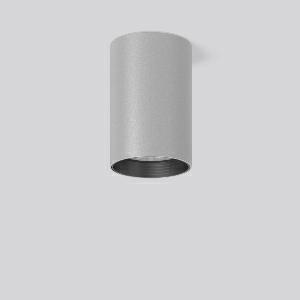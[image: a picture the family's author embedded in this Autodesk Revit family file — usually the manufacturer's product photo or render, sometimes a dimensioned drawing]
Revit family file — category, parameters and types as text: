
# Revit family: heledon_maxi_a_931229_004_3_d102
name_source: partatom
category: Lighting Fixtures
units: mm (PartAtom-declared; Revit-internal decimal feet)

## family parameters
Cut with Voids When Loaded = No
Host = Face
Light Source = No
Part Type = Normal
Room Calculation Point = No
Round Connector Dimension = Use Diameter
Shared = No

## types (1)
- HELEDON maxi A (1 x LED Modul 935, 3650 lm, 3500)
    Apparent Load = 35 VA
    Approval mark = CE
    CIE Flux Codes = 96 100 100 100 100
    Color Rendering = 92
    Color Temperature = 3500
    Default Elevation = 1800 mm
    Description = Series: HELEDON maxi
Cylindrical surface-mounted downlight. Housing: die-cast aluminium, powder-coated. Internal ceiling frame polycarbonate with bayonet mounting. Black plastic ring and recessed LED to prevent glare from the side. Optical assembly with lens made of plastic (polycarbonate) for the best homogeneous light distribution - can be changed without tools. Best colour rendering index Ra>90. Suitable for Ceiling mounting. Easy installation with a separate ceiling frame with bayonet mounting and plug connection. Driver integrated. Connected via plug-in connector. High quality converter without flickering and stroboscopic effect. The following accessories can be mounted without use of tools: interchangeable lenses, decorative glasses, honeycomb louvre, clear and frosted diffusers, white interchangeable plastic ring. 
Colour: silver
Diameter: 123 mm
Height: 183 mm
Lamp: LED
Socket: without socket
Colour temperature: 3500K
Colour rendering index (CRI): 92
System power: 35 W
Rated luminous flux: 3650 lm
Luminous efficiency: 104 lm/W
Control gear: Regulated power supply
Protection class: I
Type of protection: IP 20
    Height = 183 mm
    Lamp = 1 x LED Modul 935
    Lamp Light Flux = 3650 lm
    Lamp count = 1
    Length = 123 mm
    Lifetime = 50000 h
    Luminous efficacy = 104 lm/W
    Manufacturer = RZB
    ModVariant = No
    Model = 931229.004.3
    Mounting Place = Ceiling
    Mounting Type = Surface mounted
    Number of Poles = 1
    OnlyDefault = Yes
    Power Factor = 1
    Product Name = HELEDON maxi A
    Product group = Surface mounted downlights
    ProductGroupID = 302
    Protection Class = Protection class I
    Protection Degree = IP 20
    RLX_Detail_Level = 1
    RLX_Emergency_Light_Flux = 0 lm
    RLX_Emergency_Type = 0
    RLX_Emergency_Type_DB = No
    RlxData = <blob elided: 98057 chars, md5=a1cab5d1>
    Socket = socket
    Standby Power = 0 W
    System Light Flux = 3650 lm
    System Power = 35 W
    Type Comments = Product without accessories
    Type Image = 931193.004.jpg
    URL = http://relux.com
    VarID = ---
    Voltage = 230 V
    Voltage Range = 220-240 V
    Weight = 0.00 kg
    Width = 0 mm  [stored 0 ft]

note: [stored X ft] marks values corroborated as IEEE doubles in the binary element streams (Revit-internal decimal feet)

## geometry (parser evidence)
native form markers: Blend x4, Sweep x10
no freeform markers — native parametric forms only
